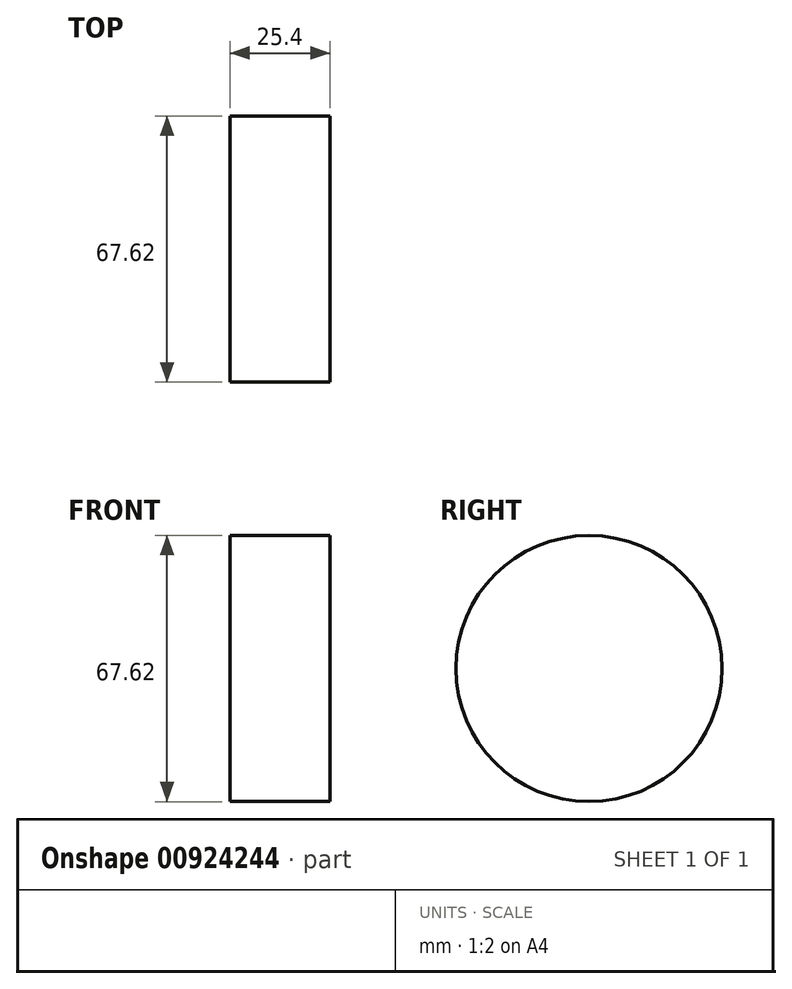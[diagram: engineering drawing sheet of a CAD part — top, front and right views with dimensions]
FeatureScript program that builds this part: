
annotation { "Feature Type Name" : "Feature", "Feature Type Description" : "" }
export const myFeature = defineFeature(function(context is Context, id is Id, definition is map)
    precondition{}
    {
        {
            var Q0;
            Q0=qCreatedBy(makeId("Right.planeOp"),FACE);
            var sketch = newSketch(context, id + "F0", { "sketchPlane" : qUnion([Q0])});
            skCircle(sketch, "E0", {"center": v(0, 0) * mm, "radius": 33.8 * mm});
            skSolve(sketch);
        }
        {
            var Q0;
            Q0=makeQuery(id+"F0.imprint","IMPRINT",FACE,{"disambiguationData":[TD([[makeQuery(id+"F0.imprint","IMPRINT",EDGE,{"derivedFrom":sQuery(id+"F0.wireOp",EDGE,"E0")}),1.0]])]});
            extrude(context, id + "F1", {"entities" : qUnion([Q0]), "depth" : 25.4 * mm, "offsetDistance" : 25.4 * mm});
        }
    });
